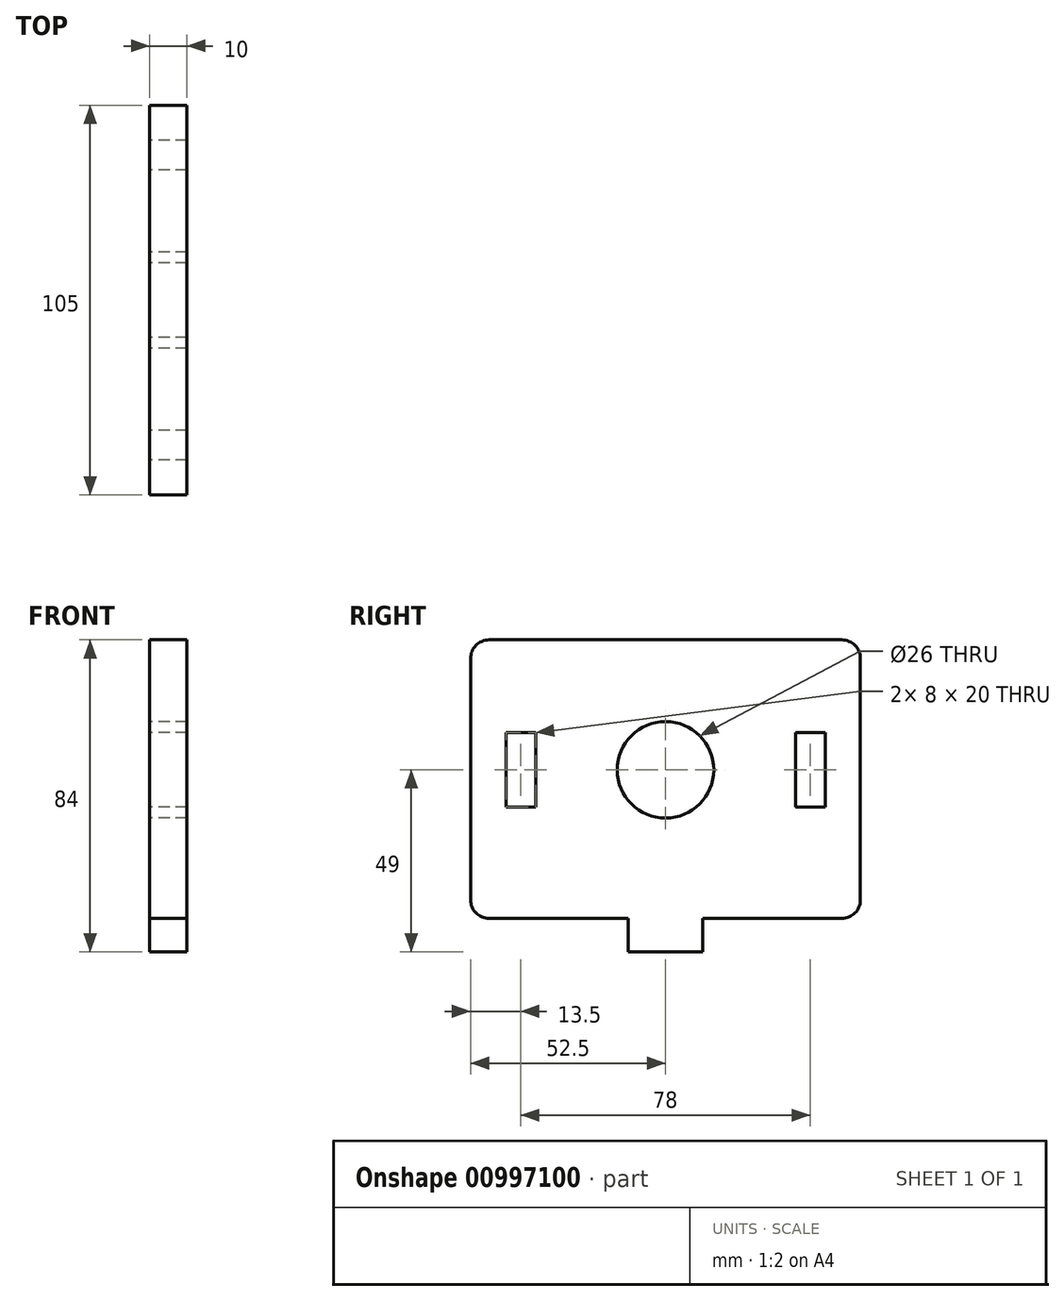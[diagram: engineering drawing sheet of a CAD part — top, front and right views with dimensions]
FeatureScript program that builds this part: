
annotation { "Feature Type Name" : "Feature", "Feature Type Description" : "" }
export const myFeature = defineFeature(function(context is Context, id is Id, definition is map)
    precondition{}
    {
        {
            var Q0;
            Q0=qCreatedBy(makeId("Right.planeOp"),FACE);
            var sketch = newSketch(context, id + "F0", { "sketchPlane" : qUnion([Q0])});
            skLineSegment(sketch, "E0.bottom", {"start": v(-47.5, 0) * mm, "end": v(-10, 0) * mm});
            skLineSegment(sketch, "E0.top", {"start": v(-47.5, 75) * mm, "end": v(47.5, 75) * mm});
            skLineSegment(sketch, "E0.left", {"start": v(-52.5, 5) * mm, "end": v(-52.5, 70) * mm});
            skLineSegment(sketch, "E0.right", {"start": v(52.5, 5) * mm, "end": v(52.5, 70) * mm});
            skLineSegment(sketch, "E1.top", {"start": v(-10, -9) * mm, "end": v(10, -9) * mm});
            skLineSegment(sketch, "E1.left", {"start": v(-10, 0) * mm, "end": v(-10, -9) * mm});
            skLineSegment(sketch, "E1.right", {"start": v(10, 0) * mm, "end": v(10, -9) * mm});
            skLineSegment(sketch, "E2.trimOffspring", {"start": v(10, 0) * mm, "end": v(47.5, 0) * mm});
            skPoint(sketch, "E3", {"position": v(0, 75) * mm});
            skPoint(sketch, "E4", {"position": v(0, -9) * mm});
            skPoint(sketch, "E5.visualSharp", {"position": v(-52.5, 0) * mm});
            skArc(sketch, "E5.filletArc", {"start": v(-52.5, 5) * mm, "mid": v(-51.04, 1.46) * mm, "end": v(-47.5, 0) * mm});
            skPoint(sketch, "E6.visualSharp", {"position": v(52.5, 0) * mm});
            skArc(sketch, "E6.filletArc", {"start": v(47.5, 0) * mm, "mid": v(51.04, 1.46) * mm, "end": v(52.5, 5) * mm});
            skPoint(sketch, "E7.visualSharp", {"position": v(-52.5, 75) * mm});
            skArc(sketch, "E7.filletArc", {"start": v(-47.5, 75) * mm, "mid": v(-51.04, 73.54) * mm, "end": v(-52.5, 70) * mm});
            skPoint(sketch, "E8.visualSharp", {"position": v(52.5, 75) * mm});
            skArc(sketch, "E8.filletArc", {"start": v(52.5, 70) * mm, "mid": v(51.04, 73.54) * mm, "end": v(47.5, 75) * mm});
            skCircle(sketch, "E9", {"center": v(0, 40) * mm, "radius": 13 * mm});
            skLineSegment(sketch, "E10.bottom", {"start": v(-43, 50) * mm, "end": v(-35, 50) * mm});
            skLineSegment(sketch, "E10.top", {"start": v(-43, 30) * mm, "end": v(-35, 30) * mm});
            skLineSegment(sketch, "E10.left", {"start": v(-43, 50) * mm, "end": v(-43, 30) * mm});
            skLineSegment(sketch, "E10.right", {"start": v(-35, 50) * mm, "end": v(-35, 30) * mm});
            skPoint(sketch, "E11", {"position": v(-35, 40) * mm});
            skPoint(sketch, "E12.MirrorP", {"position": v(35, 40) * mm});
            skLineSegment(sketch, "E13.MirrorCS", {"start": v(43, 50) * mm, "end": v(35, 50) * mm});
            skLineSegment(sketch, "E14.MirrorCS", {"start": v(35, 50) * mm, "end": v(35, 30) * mm});
            skLineSegment(sketch, "E15.MirrorCS", {"start": v(43, 30) * mm, "end": v(35, 30) * mm});
            skLineSegment(sketch, "E16.MirrorCS", {"start": v(43, 50) * mm, "end": v(43, 30) * mm});
            skSolve(sketch);
        }
        {
            var Q0;
            Q0 = qSketchRegion(id + "F0", true);
            extrude(context, id + "F1", {"entities" : qUnion([Q0]), "depth" : 10 * mm, "offsetDistance" : 25 * mm});
        }
    });
